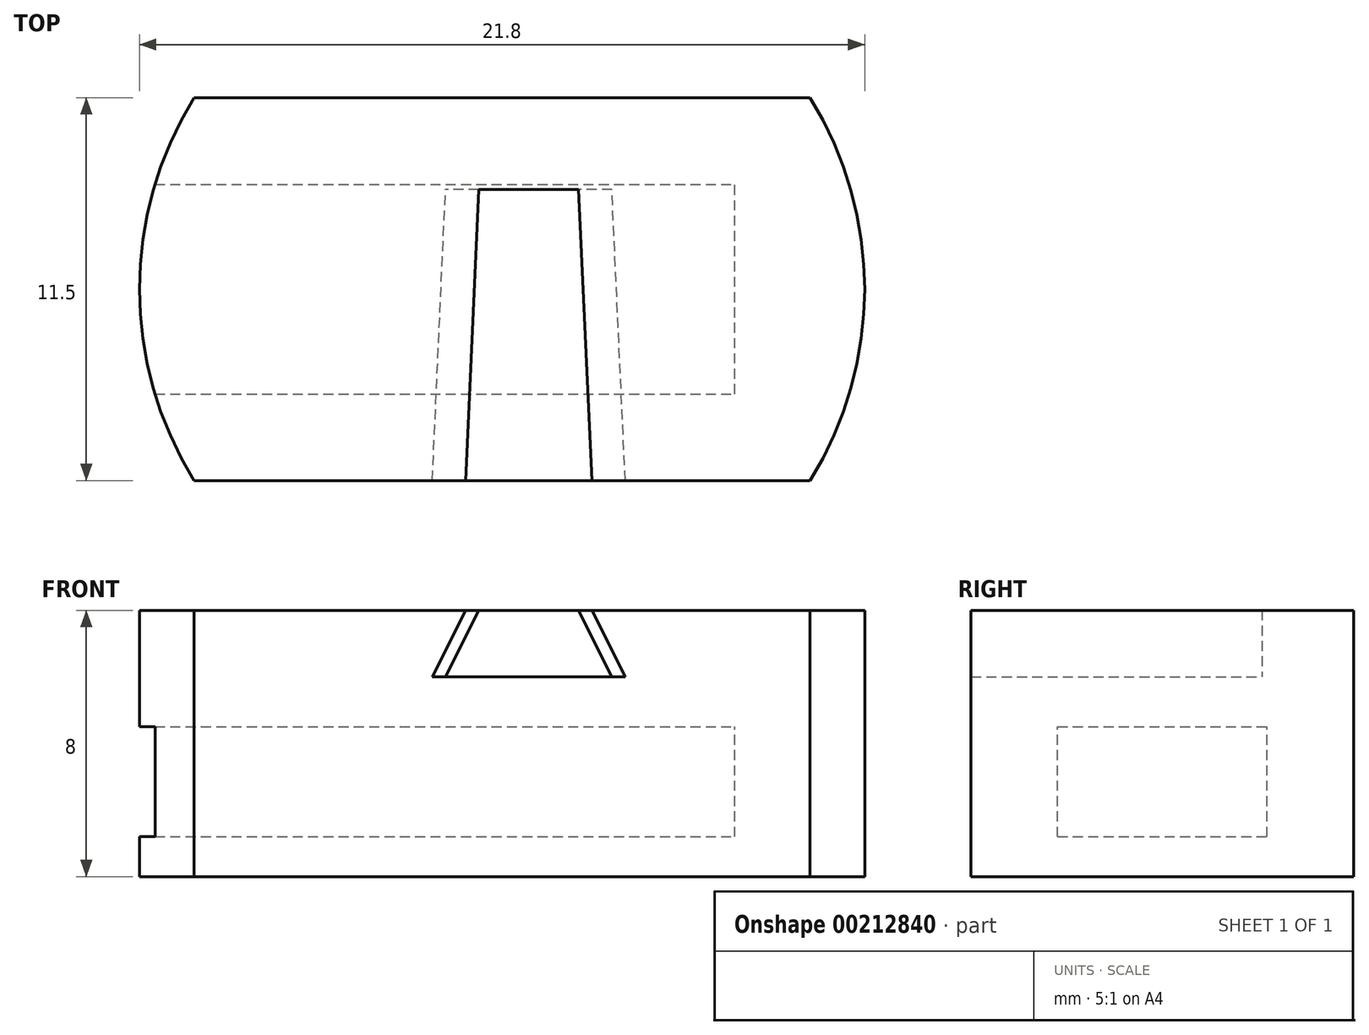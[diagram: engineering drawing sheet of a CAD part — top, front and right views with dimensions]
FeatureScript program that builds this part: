
annotation { "Feature Type Name" : "Feature", "Feature Type Description" : "" }
export const myFeature = defineFeature(function(context is Context, id is Id, definition is map)
    precondition{}
    {
        {
            var Q0;
            Q0=qCreatedBy(makeId("Top.planeOp"),FACE);
            var sketch = newSketch(context, id + "F0", { "sketchPlane" : qUnion([Q0])});
            skLineSegment(sketch, "E0.bottom", {"start": v(8.79, 5.75) * mm, "end": v(-8.79, 5.75) * mm});
            skLineSegment(sketch, "E0.top", {"start": v(8.79, -5.75) * mm, "end": v(-8.79, -5.75) * mm});
            skPoint(sketch, "E0.middle", {"position": v(0, 0) * mm});
            skArc(sketch, "E1", {"start": v(-8.79, 5.75) * mm, "mid": v(-10.5, 0) * mm, "end": v(-8.79, -5.75) * mm, "construction": true});
            skArc(sketch, "E2.trimOffspring", {"start": v(8.79, -5.75) * mm, "mid": v(10.5, 0) * mm, "end": v(8.79, 5.75) * mm, "construction": true});
            skArc(sketch, "E3.0", {"start": v(-9.26, 5.75) * mm, "mid": v(-10.9, 0) * mm, "end": v(-9.26, -5.75) * mm});
            skLineSegment(sketch, "E4", {"start": v(-8.79, -5.75) * mm, "end": v(-9.26, -5.75) * mm});
            skLineSegment(sketch, "E5", {"start": v(-8.79, 5.75) * mm, "end": v(-9.26, 5.75) * mm});
            skArc(sketch, "E6.MirrorCS", {"start": v(9.26, 5.75) * mm, "mid": v(10.9, 0) * mm, "end": v(9.26, -5.75) * mm});
            skLineSegment(sketch, "E7", {"start": v(8.79, 5.75) * mm, "end": v(9.26, 5.75) * mm});
            skLineSegment(sketch, "E8", {"start": v(8.79, -5.75) * mm, "end": v(9.26, -5.75) * mm});
            skSolve(sketch);
        }
        {
            var Q0;
            Q0=makeQuery(id+"F0.imprint","IMPRINT",FACE,{"disambiguationData":[TD([[makeQuery(id+"F0.imprint","IMPRINT",EDGE,{"derivedFrom":sQuery(id+"F0.wireOp",EDGE,"E0.bottom")}),1.0]])]});
            extrude(context, id + "F1", {"entities" : qUnion([Q0]), "oppositeDirection" : true, "depth" : 8 * mm});
        }
        {
            var Q0;
            Q0=makeQuery(id+"F1.opExtrude","SWEPT_FACE",FACE,{"disambiguationData":[OSD([sQuery(id+"F0.wireOp",EDGE,"E0.top")])]});
            var sketch = newSketch(context, id + "F2", { "sketchPlane" : qUnion([Q0])});
            skLineSegment(sketch, "E9", {"start": v(-1.1, 0) * mm, "end": v(-2.1, -2) * mm});
            skLineSegment(sketch, "E10.MirrorCS", {"start": v(2.7, 0) * mm, "end": v(3.7, -2) * mm});
            skLineSegment(sketch, "E11", {"start": v(2.7, 0) * mm, "end": v(-1.1, 0) * mm});
            skLineSegment(sketch, "E12", {"start": v(3.7, -2) * mm, "end": v(-2.1, -2) * mm});
            skLineSegment(sketch, "E13", {"start": v(0, 4.85) * mm, "end": v(0, -2.65) * mm, "construction": true});
            skSolve(sketch);
        }
        {
            var Q0;
            Q0=qCreatedBy(makeId("Front.planeOp"),FACE);
            cPlane(context, id + "F3", {"entities" : qUnion([Q0]), "cplaneType" : CPlaneType.OFFSET, "offset" : 3 * mm, "oppositeDirection" : true, "width" : 150 * mm, "height" : 150 * mm});
        }
        {
            var Q0;
            Q0=qCreatedBy(id+"F3.planeOp",FACE);
            var sketch = newSketch(context, id + "F4", { "sketchPlane" : qUnion([Q0])});
            skLineSegment(sketch, "E14.0", {"start": v(2.7, 0) * mm, "end": v(3.7, -2) * mm, "construction": true});
            skLineSegment(sketch, "E14.3", {"start": v(-1.1, 0) * mm, "end": v(-2.1, -2) * mm, "construction": true});
            skLineSegment(sketch, "E15", {"start": v(2.3, 0) * mm, "end": v(3.3, -2) * mm});
            skLineSegment(sketch, "E16.MirrorCS", {"start": v(-0.7, 0) * mm, "end": v(-1.7, -2) * mm});
            skLineSegment(sketch, "E17", {"start": v(2.3, 0) * mm, "end": v(-0.7, 0) * mm});
            skLineSegment(sketch, "E18", {"start": v(3.3, -2) * mm, "end": v(-1.7, -2) * mm});
            skSolve(sketch);
        }
        {
            var Q1;
            Q1=qSketchRegion(id+"F2",true);
            var Q2;
            Q2=qSketchRegion(id+"F4",true);
            loft(context, id + "F5", {"operationType" : NewBodyOperationType.REMOVE, "sheetProfilesArray" : [{ "sheetProfileEntities" : qUnion([Q1]) }, { "sheetProfileEntities" : qUnion([Q2]) }]});
        }
        {
            var Q0;
            Q0=qCreatedBy(makeId("Right.planeOp"),FACE);
            var sketch = newSketch(context, id + "F6", { "sketchPlane" : qUnion([Q0])});
            skLineSegment(sketch, "E19.bottom", {"start": v(-3.15, -6.8) * mm, "end": v(3.15, -6.8) * mm});
            skLineSegment(sketch, "E19.top", {"start": v(-3.15, -3.5) * mm, "end": v(3.15, -3.5) * mm});
            skLineSegment(sketch, "E19.left", {"start": v(-3.15, -6.8) * mm, "end": v(-3.15, -3.5) * mm});
            skLineSegment(sketch, "E19.right", {"start": v(3.15, -6.8) * mm, "end": v(3.15, -3.5) * mm});
            skPoint(sketch, "E19.middle", {"position": v(0, -5.15) * mm});
            skSolve(sketch);
        }
        {
            var Q0;
            Q0=qSketchRegion(id+"F6",true);
            extrude(context, id + "F7", {"entities" : qUnion([Q0]), "operationType" : NewBodyOperationType.REMOVE, "oppositeDirection" : true, "depth" : 11.9 * mm});
        }
        {
            var Q0;
            Q0=qSketchRegion(id+"F6",true);
            extrude(context, id + "F8", {"entities" : qUnion([Q0]), "operationType" : NewBodyOperationType.REMOVE, "depth" : 7 * mm});
        }
    });
